FCSTD DOCUMENT  (FreeCAD 0.18R16131 (Git))
Label: Plattform
License: All rights reserved
LicenseURL: http://en.wikipedia.org/wiki/All_rights_reserved
objects: App::Part×1, Spreadsheet::Sheet×1, Sketcher::SketchObject×1
note: 1 computed .brp shape members not serialized (recipe doc carries the construction recipe); baked Part::Feature solids carry a one-line shape summary decoded from their .brp

FEATURE [App::Part] Part
  Origin = -> Origin
FEATURE [Spreadsheet::Sheet] Spreadsheet
  cells = E1=Schlitze; A2=length; B2=330; C2=MountholeRadius; D2=3.1; E2=lenght; F2=20; A3=width; B3=200; E3=width; F3=3.1
FEATURE [Sketcher::SketchObject] Sketch
  expr: Constraints[516] = Spreadsheet.F2
  expr: Constraints[195] = Spreadsheet.F2
  expr: Constraints[4] = Spreadsheet.B2
  expr: Constraints[3] = Spreadsheet.B3
  expr: Constraints[515] = Spreadsheet.F3
  expr: Constraints[179] = Spreadsheet.F3
  expr: Constraints[20] = Spreadsheet.D2
  sketch-geometry (180):
    g0: LineSegment StartX=-200 StartY=370 StartZ=0 EndX=-200 EndY=40 EndZ=0
    g1: LineSegment StartX=-2.84e-14 StartY=370 StartZ=0 EndX=-1.137e-13 EndY=40 EndZ=0
    g2: ArcOfCircle CenterX=-100 CenterY=191.667 CenterZ=0 NormalX=0 NormalY=0 NormalZ=1 AngleXU=0 Radius=181.667 StartAngle=4.12948 EndAngle=5.2953
    g3: GeomPoint X=-100 Y=10 Z=0
    g4: ArcOfCircle CenterX=-100 CenterY=265 CenterZ=0 NormalX=0 NormalY=0 NormalZ=1 AngleXU=0 Radius=145 StartAngle=0.809784 EndAngle=2.33181
    g5: GeomPoint X=-100 Y=410 Z=0
    g6: Circle CenterX=-140.9 CenterY=65 CenterZ=0 NormalX=0 NormalY=0 NormalZ=1 AngleXU=0 Radius=3.1
    g7: Circle CenterX=-58.1 CenterY=65 CenterZ=0 NormalX=0 NormalY=0 NormalZ=1 AngleXU=0 Radius=3.1
    g8: Circle CenterX=-135 CenterY=366.2 CenterZ=0 NormalX=0 NormalY=0 NormalZ=1 AngleXU=0 Radius=3.1
    g9: Circle CenterX=-65 CenterY=366.2 CenterZ=0 NormalX=0 NormalY=0 NormalZ=1 AngleXU=0 Radius=3.1
    g10: Circle CenterX=-114 CenterY=195.2 CenterZ=0 NormalX=0 NormalY=0 NormalZ=1 AngleXU=0 Radius=2.1
    g11: Circle CenterX=-74 CenterY=195.2 CenterZ=0 NormalX=0 NormalY=0 NormalZ=1 AngleXU=0 Radius=10
    g12: LineSegment StartX=-180 StartY=310 StartZ=0 EndX=-160 EndY=310 EndZ=0
    g13: LineSegment StartX=-160 StartY=310 StartZ=0 EndX=-160 EndY=306.9 EndZ=0
    g14: LineSegment StartX=-160 StartY=306.9 StartZ=0 EndX=-180 EndY=306.9 EndZ=0
    g15: LineSegment StartX=-180 StartY=306.9 StartZ=0 EndX=-180 EndY=310 EndZ=0
    g16: LineSegment StartX=-40 StartY=310 StartZ=0 EndX=-20 EndY=310 EndZ=0
    g17: LineSegment StartX=-20 StartY=310 StartZ=0 EndX=-20 EndY=306.9 EndZ=0
    g18: LineSegment StartX=-20 StartY=306.9 StartZ=0 EndX=-40 EndY=306.9 EndZ=0
    g19: LineSegment StartX=-40 StartY=306.9 StartZ=0 EndX=-40 EndY=310 EndZ=0
    g20: LineSegment StartX=-180 StartY=280 StartZ=0 EndX=-160 EndY=280 EndZ=0
    g21: LineSegment StartX=-160 StartY=280 StartZ=0 EndX=-160 EndY=276.9 EndZ=0
    g22: LineSegment StartX=-160 StartY=276.9 StartZ=0 EndX=-180 EndY=276.9 EndZ=0
    g23: LineSegment StartX=-180 StartY=276.9 StartZ=0 EndX=-180 EndY=280 EndZ=0
    g24: LineSegment StartX=-180 StartY=340 StartZ=0 EndX=-160 EndY=340 EndZ=0
    g25: LineSegment StartX=-160 StartY=340 StartZ=0 EndX=-160 EndY=336.9 EndZ=0
    g26: LineSegment StartX=-160 StartY=336.9 StartZ=0 EndX=-180 EndY=336.9 EndZ=0
    g27: LineSegment StartX=-180 StartY=336.9 StartZ=0 EndX=-180 EndY=340 EndZ=0
    g28: LineSegment StartX=-40 StartY=340 StartZ=0 EndX=-20 EndY=340 EndZ=0
    g29: LineSegment StartX=-20 StartY=340 StartZ=0 EndX=-20 EndY=336.9 EndZ=0
    g30: LineSegment StartX=-20 StartY=336.9 StartZ=0 EndX=-40 EndY=336.9 EndZ=0
    g31: LineSegment StartX=-40 StartY=336.9 StartZ=0 EndX=-40 EndY=340 EndZ=0
    g32: LineSegment StartX=-40 StartY=280 StartZ=0 EndX=-20 EndY=280 EndZ=0
    g33: LineSegment StartX=-20 StartY=280 StartZ=0 EndX=-20 EndY=276.9 EndZ=0
    g34: LineSegment StartX=-20 StartY=276.9 StartZ=0 EndX=-40 EndY=276.9 EndZ=0
    g35: LineSegment StartX=-40 StartY=276.9 StartZ=0 EndX=-40 EndY=280 EndZ=0
    g36: LineSegment StartX=-180 StartY=370 StartZ=0 EndX=-160 EndY=370 EndZ=0
    g37: LineSegment StartX=-160 StartY=370 StartZ=0 EndX=-160 EndY=366.9 EndZ=0
    g38: LineSegment StartX=-160 StartY=366.9 StartZ=0 EndX=-180 EndY=366.9 EndZ=0
    g39: LineSegment StartX=-180 StartY=366.9 StartZ=0 EndX=-180 EndY=370 EndZ=0
    g40: LineSegment StartX=-40 StartY=370 StartZ=0 EndX=-20 EndY=370 EndZ=0
    g41: LineSegment StartX=-20 StartY=370 StartZ=0 EndX=-20 EndY=366.9 EndZ=0
    g42: LineSegment StartX=-20 StartY=366.9 StartZ=0 EndX=-40 EndY=366.9 EndZ=0
    g43: LineSegment StartX=-40 StartY=366.9 StartZ=0 EndX=-40 EndY=370 EndZ=0
    g44: LineSegment StartX=-180 StartY=250 StartZ=0 EndX=-160 EndY=250 EndZ=0
    g45: LineSegment StartX=-160 StartY=250 StartZ=0 EndX=-160 EndY=246.9 EndZ=0
    g46: LineSegment StartX=-160 StartY=246.9 StartZ=0 EndX=-180 EndY=246.9 EndZ=0
    g47: LineSegment StartX=-180 StartY=246.9 StartZ=0 EndX=-180 EndY=250 EndZ=0
    g48: LineSegment StartX=-40 StartY=246.9 StartZ=0 EndX=-20 EndY=246.9 EndZ=0
    g49: LineSegment StartX=-20 StartY=246.9 StartZ=0 EndX=-20 EndY=250 EndZ=0
    g50: LineSegment StartX=-20 StartY=250 StartZ=0 EndX=-40 EndY=250 EndZ=0
    g51: LineSegment StartX=-40 StartY=250 StartZ=0 EndX=-40 EndY=246.9 EndZ=0
    g52: LineSegment StartX=-180 StartY=220 StartZ=0 EndX=-160 EndY=220 EndZ=0
    g53: LineSegment StartX=-160 StartY=220 StartZ=0 EndX=-160 EndY=216.9 EndZ=0
    g54: LineSegment StartX=-160 StartY=216.9 StartZ=0 EndX=-180 EndY=216.9 EndZ=0
    g55: LineSegment StartX=-180 StartY=216.9 StartZ=0 EndX=-180 EndY=220 EndZ=0
    g56: LineSegment StartX=-40 StartY=220 StartZ=0 EndX=-20 EndY=220 EndZ=0
    g57: LineSegment StartX=-20 StartY=220 StartZ=0 EndX=-20 EndY=216.9 EndZ=0
    g58: LineSegment StartX=-20 StartY=216.9 StartZ=0 EndX=-40 EndY=216.9 EndZ=0
    g59: LineSegment StartX=-40 StartY=216.9 StartZ=0 EndX=-40 EndY=220 EndZ=0
    g60: LineSegment StartX=-180 StartY=190 StartZ=0 EndX=-160 EndY=190 EndZ=0
    g61: LineSegment StartX=-160 StartY=190 StartZ=0 EndX=-160 EndY=186.9 EndZ=0
    g62: LineSegment StartX=-160 StartY=186.9 StartZ=0 EndX=-180 EndY=186.9 EndZ=0
    g63: LineSegment StartX=-180 StartY=186.9 StartZ=0 EndX=-180 EndY=190 EndZ=0
    g64: LineSegment StartX=-40 StartY=190 StartZ=0 EndX=-20 EndY=190 EndZ=0
    g65: LineSegment StartX=-20 StartY=190 StartZ=0 EndX=-20 EndY=186.9 EndZ=0
    g66: LineSegment StartX=-20 StartY=186.9 StartZ=0 EndX=-40 EndY=186.9 EndZ=0
    g67: LineSegment StartX=-40 StartY=186.9 StartZ=0 EndX=-40 EndY=190 EndZ=0
    g68: LineSegment StartX=-180 StartY=160 StartZ=0 EndX=-160 EndY=160 EndZ=0
    g69: LineSegment StartX=-160 StartY=160 StartZ=0 EndX=-160 EndY=156.9 EndZ=0
    g70: LineSegment StartX=-160 StartY=156.9 StartZ=0 EndX=-180 EndY=156.9 EndZ=0
    g71: LineSegment StartX=-180 StartY=156.9 StartZ=0 EndX=-180 EndY=160 EndZ=0
    g72: LineSegment StartX=-40 StartY=160 StartZ=0 EndX=-20 EndY=160 EndZ=0
    g73: LineSegment StartX=-20 StartY=160 StartZ=0 EndX=-20 EndY=156.9 EndZ=0
    g74: LineSegment StartX=-20 StartY=156.9 StartZ=0 EndX=-40 EndY=156.9 EndZ=0
    g75: LineSegment StartX=-40 StartY=156.9 StartZ=0 EndX=-40 EndY=160 EndZ=0
    g76: LineSegment StartX=-180 StartY=40 StartZ=0 EndX=-160 EndY=40 EndZ=0
    g77: LineSegment StartX=-160 StartY=40 StartZ=0 EndX=-160 EndY=36.9 EndZ=0
    g78: LineSegment StartX=-160 StartY=36.9 StartZ=0 EndX=-180 EndY=36.9 EndZ=0
    g79: LineSegment StartX=-180 StartY=36.9 StartZ=0 EndX=-180 EndY=40 EndZ=0
    g80: LineSegment StartX=-40 StartY=40 StartZ=0 EndX=-20 EndY=40 EndZ=0
    g81: LineSegment StartX=-20 StartY=40 StartZ=0 EndX=-20 EndY=36.9 EndZ=0
    g82: LineSegment StartX=-20 StartY=36.9 StartZ=0 EndX=-40 EndY=36.9 EndZ=0
    g83: LineSegment StartX=-40 StartY=36.9 StartZ=0 EndX=-40 EndY=40 EndZ=0
    g84: LineSegment StartX=-180 StartY=130 StartZ=0 EndX=-160 EndY=130 EndZ=0
    g85: LineSegment StartX=-160 StartY=130 StartZ=0 EndX=-160 EndY=126.9 EndZ=0
    g86: LineSegment StartX=-160 StartY=126.9 StartZ=0 EndX=-180 EndY=126.9 EndZ=0
    g87: LineSegment StartX=-180 StartY=126.9 StartZ=0 EndX=-180 EndY=130 EndZ=0
    g88: LineSegment StartX=-180 StartY=100 StartZ=0 EndX=-160 EndY=100 EndZ=0
    g89: LineSegment StartX=-160 StartY=100 StartZ=0 EndX=-160 EndY=96.9 EndZ=0
    g90: LineSegment StartX=-160 StartY=96.9 StartZ=0 EndX=-180 EndY=96.9 EndZ=0
    g91: LineSegment StartX=-180 StartY=96.9 StartZ=0 EndX=-180 EndY=100 EndZ=0
    g92: LineSegment StartX=-180 StartY=70 StartZ=0 EndX=-160 EndY=70 EndZ=0
    g93: LineSegment StartX=-160 StartY=70 StartZ=0 EndX=-160 EndY=66.9 EndZ=0
    g94: LineSegment StartX=-160 StartY=66.9 StartZ=0 EndX=-180 EndY=66.9 EndZ=0
    g95: LineSegment StartX=-180 StartY=66.9 StartZ=0 EndX=-180 EndY=70 EndZ=0
    g96: LineSegment StartX=-40 StartY=130 StartZ=0 EndX=-20 EndY=130 EndZ=0
    g97: LineSegment StartX=-20 StartY=130 StartZ=0 EndX=-20 EndY=126.9 EndZ=0
    g98: LineSegment StartX=-20 StartY=126.9 StartZ=0 EndX=-40 EndY=126.9 EndZ=0
    g99: LineSegment StartX=-40 StartY=126.9 StartZ=0 EndX=-40 EndY=130 EndZ=0
    g100: LineSegment StartX=-40 StartY=100 StartZ=0 EndX=-20 EndY=100 EndZ=0
    g101: LineSegment StartX=-20 StartY=100 StartZ=0 EndX=-20 EndY=96.9 EndZ=0
    g102: LineSegment StartX=-20 StartY=96.9 StartZ=0 EndX=-40 EndY=96.9 EndZ=0
    g103: LineSegment StartX=-40 StartY=96.9 StartZ=0 EndX=-40 EndY=100 EndZ=0
    g104: LineSegment StartX=-40 StartY=70 StartZ=0 EndX=-20 EndY=70 EndZ=0
    g105: LineSegment StartX=-20 StartY=70 StartZ=0 EndX=-20 EndY=66.9 EndZ=0
    g106: LineSegment StartX=-20 StartY=66.9 StartZ=0 EndX=-40 EndY=66.9 EndZ=0
    g107: LineSegment StartX=-40 StartY=66.9 StartZ=0 EndX=-40 EndY=70 EndZ=0
    g108: LineSegment StartX=-116.55 StartY=40 StartZ=0 EndX=-113.45 EndY=40 EndZ=0
    g109: LineSegment StartX=-113.45 StartY=40 StartZ=0 EndX=-113.45 EndY=20 EndZ=0
    g110: LineSegment StartX=-113.45 StartY=20 StartZ=0 EndX=-116.55 EndY=20 EndZ=0
    g111: LineSegment StartX=-116.55 StartY=20 StartZ=0 EndX=-116.55 EndY=40 EndZ=0
    g112: LineSegment StartX=-86.55 StartY=40 StartZ=0 EndX=-83.45 EndY=40 EndZ=0
    g113: LineSegment StartX=-83.45 StartY=40 StartZ=0 EndX=-83.45 EndY=20 EndZ=0
    g114: LineSegment StartX=-83.45 StartY=20 StartZ=0 EndX=-86.55 EndY=20 EndZ=0
    g115: LineSegment StartX=-86.55 StartY=20 StartZ=0 EndX=-86.55 EndY=40 EndZ=0
    g116: LineSegment StartX=-116.55 StartY=90 StartZ=0 EndX=-113.45 EndY=90 EndZ=0
    g117: LineSegment StartX=-113.45 StartY=90 StartZ=0 EndX=-113.45 EndY=70 EndZ=0
    g118: LineSegment StartX=-113.45 StartY=70 StartZ=0 EndX=-116.55 EndY=70 EndZ=0
    g119: LineSegment StartX=-116.55 StartY=70 StartZ=0 EndX=-116.55 EndY=90 EndZ=0
    g120: LineSegment StartX=-116.55 StartY=140 StartZ=0 EndX=-113.45 EndY=140 EndZ=0
    g121: LineSegment StartX=-113.45 StartY=140 StartZ=0 EndX=-113.45 EndY=120 EndZ=0
    g122: LineSegment StartX=-113.45 StartY=120 StartZ=0 EndX=-116.55 EndY=120 EndZ=0
    g123: LineSegment StartX=-116.55 StartY=120 StartZ=0 EndX=-116.55 EndY=140 EndZ=0
    g124: LineSegment StartX=-116.55 StartY=190 StartZ=0 EndX=-113.45 EndY=190 EndZ=0
    g125: LineSegment StartX=-113.45 StartY=190 StartZ=0 EndX=-113.45 EndY=170 EndZ=0
    g126: LineSegment StartX=-113.45 StartY=170 StartZ=0 EndX=-116.55 EndY=170 EndZ=0
    g127: LineSegment StartX=-116.55 StartY=170 StartZ=0 EndX=-116.55 EndY=190 EndZ=0
    g128: LineSegment StartX=-86.55 StartY=90 StartZ=0 EndX=-83.45 EndY=90 EndZ=0
    g129: LineSegment StartX=-83.45 StartY=90 StartZ=0 EndX=-83.45 EndY=70 EndZ=0
    g130: LineSegment StartX=-83.45 StartY=70 StartZ=0 EndX=-86.55 EndY=70 EndZ=0
    g131: LineSegment StartX=-86.55 StartY=70 StartZ=0 EndX=-86.55 EndY=90 EndZ=0
    g132: LineSegment StartX=-86.55 StartY=140 StartZ=0 EndX=-83.45 EndY=140 EndZ=0
    g133: LineSegment StartX=-83.45 StartY=140 StartZ=0 EndX=-83.45 EndY=120 EndZ=0
    g134: LineSegment StartX=-83.45 StartY=120 StartZ=0 EndX=-86.55 EndY=120 EndZ=0
    g135: LineSegment StartX=-86.55 StartY=120 StartZ=0 EndX=-86.55 EndY=140 EndZ=0
    g136: LineSegment StartX=-86.55 StartY=190 StartZ=0 EndX=-83.45 EndY=190 EndZ=0
    g137: LineSegment StartX=-83.45 StartY=190 StartZ=0 EndX=-83.45 EndY=170 EndZ=0
    g138: LineSegment StartX=-83.45 StartY=170 StartZ=0 EndX=-86.55 EndY=170 EndZ=0
    g139: LineSegment StartX=-86.55 StartY=170 StartZ=0 EndX=-86.55 EndY=190 EndZ=0
    g140: LineSegment StartX=-116.55 StartY=270 StartZ=0 EndX=-113.45 EndY=270 EndZ=0
    g141: LineSegment StartX=-113.45 StartY=270 StartZ=0 EndX=-113.45 EndY=250 EndZ=0
    g142: LineSegment StartX=-113.45 StartY=250 StartZ=0 EndX=-116.55 EndY=250 EndZ=0
    g143: LineSegment StartX=-116.55 StartY=250 StartZ=0 EndX=-116.55 EndY=270 EndZ=0
    g144: LineSegment StartX=-86.55 StartY=270 StartZ=0 EndX=-83.45 EndY=270 EndZ=0
    g145: LineSegment StartX=-83.45 StartY=270 StartZ=0 EndX=-83.45 EndY=250 EndZ=0
    g146: LineSegment StartX=-83.45 StartY=250 StartZ=0 EndX=-86.55 EndY=250 EndZ=0
    g147: LineSegment StartX=-86.55 StartY=250 StartZ=0 EndX=-86.55 EndY=270 EndZ=0
    g148: LineSegment StartX=-116.55 StartY=320 StartZ=0 EndX=-113.45 EndY=320 EndZ=0
    g149: LineSegment StartX=-113.45 StartY=320 StartZ=0 EndX=-113.45 EndY=300 EndZ=0
    g150: LineSegment StartX=-113.45 StartY=300 StartZ=0 EndX=-116.55 EndY=300 EndZ=0
    g151: LineSegment StartX=-116.55 StartY=300 StartZ=0 EndX=-116.55 EndY=320 EndZ=0
    g152: LineSegment StartX=-86.55 StartY=320 StartZ=0 EndX=-83.45 EndY=320 EndZ=0
    g153: LineSegment StartX=-83.45 StartY=320 StartZ=0 EndX=-83.45 EndY=300 EndZ=0
    g154: LineSegment StartX=-83.45 StartY=300 StartZ=0 EndX=-86.55 EndY=300 EndZ=0
    g155: LineSegment StartX=-86.55 StartY=300 StartZ=0 EndX=-86.55 EndY=320 EndZ=0
    g156: LineSegment StartX=-116.55 StartY=405 StartZ=0 EndX=-113.45 EndY=405 EndZ=0
    g157: LineSegment StartX=-113.45 StartY=405 StartZ=0 EndX=-113.45 EndY=385 EndZ=0
    g158: LineSegment StartX=-113.45 StartY=385 StartZ=0 EndX=-116.55 EndY=385 EndZ=0
    g159: LineSegment StartX=-116.55 StartY=385 StartZ=0 EndX=-116.55 EndY=405 EndZ=0
    g160: LineSegment StartX=-86.55 StartY=405 StartZ=0 EndX=-83.45 EndY=405 EndZ=0
    g161: LineSegment StartX=-83.45 StartY=405 StartZ=0 EndX=-83.45 EndY=385 EndZ=0
    g162: LineSegment StartX=-83.45 StartY=385 StartZ=0 EndX=-86.55 EndY=385 EndZ=0
    g163: LineSegment StartX=-86.55 StartY=385 StartZ=0 EndX=-86.55 EndY=405 EndZ=0
    g164: LineSegment StartX=-116.55 StartY=370 StartZ=0 EndX=-113.45 EndY=370 EndZ=0
    g165: LineSegment StartX=-113.45 StartY=370 StartZ=0 EndX=-113.45 EndY=350 EndZ=0
    g166: LineSegment StartX=-113.45 StartY=350 StartZ=0 EndX=-116.55 EndY=350 EndZ=0
    g167: LineSegment StartX=-116.55 StartY=350 StartZ=0 EndX=-116.55 EndY=370 EndZ=0
    g168: LineSegment StartX=-86.55 StartY=370 StartZ=0 EndX=-83.45 EndY=370 EndZ=0
    g169: LineSegment StartX=-83.45 StartY=370 StartZ=0 EndX=-83.45 EndY=350 EndZ=0
    g170: LineSegment StartX=-83.45 StartY=350 StartZ=0 EndX=-86.55 EndY=350 EndZ=0
    g171: LineSegment StartX=-86.55 StartY=350 StartZ=0 EndX=-86.55 EndY=370 EndZ=0
    g172: LineSegment StartX=-150 StartY=399.183 StartZ=0 EndX=-50 EndY=399.183 EndZ=0
    g173: LineSegment StartX=-150 StartY=396.183 StartZ=0 EndX=-50 EndY=396.183 EndZ=0
    g174: LineSegment StartX=-150 StartY=399.183 StartZ=0 EndX=-150 EndY=396.183 EndZ=0
    g175: LineSegment StartX=-50 StartY=399.183 StartZ=0 EndX=-50 EndY=396.183 EndZ=0
    g176: LineSegment StartX=-199.37 StartY=369.621 StartZ=0 EndX=-198.001 EndY=367.341 EndZ=0
    g177: LineSegment StartX=-199.37 StartY=369.621 StartZ=0 EndX=-151.545 EndY=398.755 EndZ=0
    g178: LineSegment StartX=-198.001 StartY=367.341 StartZ=0 EndX=-150 EndY=396.183 EndZ=0
    g179: LineSegment StartX=-151.545 StartY=398.755 StartZ=0 EndX=-150 EndY=396.183 EndZ=0
  constraints (538):
    c: Parallel(g1,g0)
    c: Angle(g1) = -1.5708
    c: DistanceX(g1,g-1) = 0
    c: DistanceX(g0,g1) = 200
    c: DistanceY(g1,g1) = 330
    c: DistanceY(g-1,g1) = 40
    c: DistanceY(g0,g1) = 0
    c: Coincident(g2,g0)
    c: Coincident(g2,g1)
    c: PointOnObject(g3,g2)
    c: DistanceY(g-1,g3) = 10
    c: DistanceX(g3,g-1) = 100
    c: Coincident(g4,g0)
    c: Coincident(g4,g1)
    c: PointOnObject(g5,g4)
    c: DistanceX(g5,g-1) = 100
    c: DistanceY(g1,g5) = 40
    c: Equal(g6,g8)
    c: Equal(g8,g9)
    c: Equal(g9,g7)
    c: Radius(g6) = 3.1
    c: DistanceX(g6,g7) = 82.8
    c: DistanceX(g3,g7) = 41.9
    c: DistanceY(g1,g7) = 25
    c: DistanceY(g7,g6) = 0
    c: DistanceX(g8,g9) = 70
    c: DistanceY(g8,g9) = 0
    c: DistanceX(g3,g9) = 35
    c: DistanceY(g6,g8) = 301.2
    c: Radius(g10) = 2.1
    c: DistanceX(g0,g10) = 86
    c: DistanceY(g6,g10) = 130.2
    c: Radius(g11) = 10
    c: DistanceY(g11,g10) = 0
    c: DistanceX(g10,g11) = 40
    c: Coincident(g12,g13)
    c: Coincident(g13,g14)
    c: Coincident(g14,g15)
    c: Coincident(g15,g12)
    c: Horizontal(g12)
    c: Horizontal(g14)
    c: Vertical(g13)
    c: Vertical(g15)
    c: Coincident(g16,g17)
    c: Coincident(g17,g18)
    c: Coincident(g18,g19)
    c: Coincident(g19,g16)
    c: Horizontal(g16)
    c: Horizontal(g18)
    c: Vertical(g17)
    c: Vertical(g19)
    c: Coincident(g20,g21)
    c: Coincident(g21,g22)
    c: Coincident(g22,g23)
    c: Coincident(g23,g20)
    c: Horizontal(g20)
    c: Horizontal(g22)
    c: Vertical(g21)
    c: Vertical(g23)
    c: Coincident(g24,g25)
    c: Coincident(g25,g26)
    c: Coincident(g26,g27)
    c: Coincident(g27,g24)
    c: Horizontal(g24)
    c: Horizontal(g26)
    c: Vertical(g25)
    c: Vertical(g27)
    c: Coincident(g28,g29)
    c: Coincident(g29,g30)
    c: Coincident(g30,g31)
    c: Coincident(g31,g28)
    c: Horizontal(g28)
    c: Horizontal(g30)
    c: Vertical(g29)
    c: Vertical(g31)
    c: Coincident(g32,g33)
    c: Coincident(g33,g34)
    c: Coincident(g34,g35)
    c: Coincident(g35,g32)
    c: Horizontal(g32)
    c: Horizontal(g34)
    c: Vertical(g33)
    c: Vertical(g35)
    c: Coincident(g36,g37)
    c: Coincident(g37,g38)
    c: Coincident(g38,g39)
    c: Coincident(g39,g36)
    c: Horizontal(g36)
    c: Horizontal(g38)
    c: Vertical(g37)
    c: Vertical(g39)
    c: Coincident(g40,g41)
    c: Coincident(g41,g42)
    c: Coincident(g42,g43)
    c: Coincident(g43,g40)
    c: Horizontal(g40)
    c: Horizontal(g42)
    c: Vertical(g41)
    c: Vertical(g43)
    c: Coincident(g44,g45)
    c: Coincident(g45,g46)
    c: Coincident(g46,g47)
    c: Coincident(g47,g44)
    c: Horizontal(g44)
    c: Horizontal(g46)
    c: Vertical(g45)
    c: Vertical(g47)
    c: Coincident(g48,g49)
    c: Coincident(g49,g50)
    c: Coincident(g50,g51)
    c: Coincident(g51,g48)
    c: Horizontal(g48)
    c: Horizontal(g50)
    c: Vertical(g49)
    c: Vertical(g51)
    c: Coincident(g52,g53)
    c: Coincident(g53,g54)
    c: Coincident(g54,g55)
    c: Coincident(g55,g52)
    c: Horizontal(g52)
    c: Horizontal(g54)
    c: Vertical(g53)
    c: Vertical(g55)
    c: Coincident(g56,g57)
    c: Coincident(g57,g58)
    c: Coincident(g58,g59)
    c: Coincident(g59,g56)
    c: Horizontal(g56)
    c: Horizontal(g58)
    c: Vertical(g57)
    c: Vertical(g59)
    c: Coincident(g60,g61)
    c: Coincident(g61,g62)
    c: Coincident(g62,g63)
    c: Coincident(g63,g60)
    c: Horizontal(g60)
    c: Horizontal(g62)
    c: Vertical(g61)
    c: Vertical(g63)
    c: Coincident(g64,g65)
    c: Coincident(g65,g66)
    c: Coincident(g66,g67)
    c: Coincident(g67,g64)
    c: Horizontal(g64)
    c: Horizontal(g66)
    c: Vertical(g65)
    c: Vertical(g67)
    c: Coincident(g68,g69)
    c: Coincident(g69,g70)
    c: Coincident(g70,g71)
    c: Coincident(g71,g68)
    c: Horizontal(g68)
    c: Horizontal(g70)
    c: Vertical(g69)
    c: Vertical(g71)
    c: Coincident(g72,g73)
    c: Coincident(g73,g74)
    c: Coincident(g74,g75)
    c: Coincident(g75,g72)
    c: Horizontal(g72)
    c: Horizontal(g74)
    c: Vertical(g73)
    c: Vertical(g75)
    c: Coincident(g76,g77)
    c: Coincident(g77,g78)
    c: Coincident(g78,g79)
    c: Coincident(g79,g76)
    c: Horizontal(g76)
    c: Horizontal(g78)
    c: Vertical(g77)
    c: Vertical(g79)
    c: Coincident(g80,g81)
    c: Coincident(g81,g82)
    c: Coincident(g82,g83)
    c: Coincident(g83,g80)
    c: Horizontal(g80)
    c: Horizontal(g82)
    c: Vertical(g81)
    c: Vertical(g83)
    c: DistanceY(g39,g39) = 3.1
    c: Equal(g39,g27)
    c: Equal(g27,g15)
    c: Equal(g15,g43)
    c: Equal(g43,g31)
    c: Equal(g31,g19)
    c: Equal(g19,g35)
    c: Equal(g35,g23)
    c: Equal(g23,g47)
    c: Equal(g47,g51)
    c: Equal(g51,g55)
    c: Equal(g55,g59)
    c: Equal(g59,g63)
    c: Equal(g63,g67)
    c: Equal(g67,g71)
    c: Equal(g71,g75)
    c: DistanceX(g36,g36) = 20
    c: Equal(g36,g40)
    c: Equal(g40,g24)
    c: Equal(g24,g28)
    c: Equal(g28,g12)
    c: Equal(g12,g16)
    c: Equal(g16,g20)
    c: Equal(g20,g32)
    c: Equal(g32,g44)
    c: Equal(g44,g48)
    c: Equal(g48,g52)
    c: Equal(g52,g56)
    c: Equal(g56,g60)
    c: Equal(g60,g64)
    c: Equal(g64,g68)
    c: Equal(g68,g72)
    c: Equal(g72,g76)
    c: Equal(g76,g80)
    c: Equal(g71,g79)
    c: Equal(g79,g83)
    c: DistanceX(g0,g38) = 20
    c: DistanceX(g38,g26) = 0
    c: DistanceX(g26,g14) = 0
    c: DistanceX(g14,g22) = 0
    c: DistanceX(g22,g46) = 0
    c: DistanceX(g46,g54) = 0
    c: DistanceX(g54,g62) = 0
    c: DistanceX(g62,g70) = 0
    c: DistanceX(g70,g78) = 0
    c: DistanceX(g41,g1) = 20
    c: DistanceX(g29,g41) = 0
    c: DistanceX(g17,g29) = 0
    c: DistanceX(g33,g17) = 0
    c: DistanceX(g49,g33) = 0
    c: DistanceX(g57,g49) = 0
    c: DistanceX(g65,g57) = 0
    c: DistanceX(g73,g65) = 0
    c: DistanceY(g36,g0) = 0
    c: DistanceY(g40,g1) = 0
    c: DistanceY(g24,g36) = 30
    c: DistanceY(g20,g12) = 30
    c: DistanceY(g44,g20) = 30
    c: DistanceY(g52,g44) = 30
    c: DistanceY(g60,g52) = 30
    c: DistanceY(g68,g60) = 30
    c: DistanceY(g28,g40) = 30
    c: DistanceY(g16,g28) = 30
    c: DistanceY(g32,g16) = 30
    c: DistanceY(g64,g56) = 30
    c: DistanceY(g56,g49) = 30
    c: DistanceY(g72,g64) = 30
    c: DistanceY(g49,g32) = 30
    c: DistanceY(g12,g24) = 30
    c: Coincident(g84,g85)
    c: Coincident(g85,g86)
    c: Coincident(g86,g87)
    c: Coincident(g87,g84)
    c: Horizontal(g84)
    c: Horizontal(g86)
    c: Vertical(g85)
    c: Vertical(g87)
    c: Coincident(g88,g89)
    c: Coincident(g89,g90)
    c: Coincident(g90,g91)
    c: Coincident(g91,g88)
    c: Horizontal(g88)
    c: Horizontal(g90)
    c: Vertical(g89)
    c: Vertical(g91)
    c: Coincident(g92,g93)
    c: Coincident(g93,g94)
    c: Coincident(g94,g95)
    c: Coincident(g95,g92)
    c: Horizontal(g92)
    c: Horizontal(g94)
    c: Vertical(g93)
    c: Vertical(g95)
    c: Coincident(g96,g97)
    c: Coincident(g97,g98)
    c: Coincident(g98,g99)
    c: Coincident(g99,g96)
    c: Horizontal(g96)
    c: Horizontal(g98)
    c: Vertical(g97)
    c: Vertical(g99)
    c: Coincident(g100,g101)
    c: Coincident(g101,g102)
    c: Coincident(g102,g103)
    c: Coincident(g103,g100)
    c: Horizontal(g100)
    c: Vertical(g101)
    c: Vertical(g103)
    c: Coincident(g104,g105)
    c: Coincident(g105,g106)
    c: Coincident(g106,g107)
    c: Coincident(g107,g104)
    c: Horizontal(g104)
    c: Horizontal(g106)
    c: Vertical(g105)
    c: Vertical(g107)
    c: Equal(g75,g99)
    c: Equal(g99,g103)
    c: Equal(g95,g91)
    c: Equal(g91,g87)
    c: Equal(g68,g84)
    c: Equal(g84,g88)
    c: Equal(g88,g96)
    c: Equal(g96,g100)
    c: Equal(g104,g92)
    c: DistanceX(g68,g84) = 0
    c: DistanceX(g84,g88) = 0
    c: DistanceX(g88,g92) = 0
    c: DistanceX(g96,g72) = 0
    c: DistanceX(g100,g96) = 0
    c: DistanceY(g96,g72) = 30
    c: DistanceY(g100,g96) = 30
    c: DistanceY(g104,g100) = 30
    c: DistanceY(g80,g104) = 30
    c: DistanceY(g84,g68) = 30
    c: DistanceY(g88,g84) = 30
    c: DistanceY(g92,g88) = 30
    c: Equal(g105,g81)
    c: Equal(g81,g101)
    c: DistanceX(g104,g100) = 0
    c: DistanceX(g104,g80) = 0
    c: Equal(g104,g100)
    c: DistanceY(g0,g1) = 0
    c: DistanceY(g76,g92) = 30
    c: Equal(g91,g87)
    c: Equal(g89,g61)
    c: Coincident(g108,g109)
    c: Coincident(g109,g110)
    c: Coincident(g110,g111)
    c: Coincident(g111,g108)
    c: Horizontal(g108)
    c: Horizontal(g110)
    c: Vertical(g109)
    c: Vertical(g111)
    c: Coincident(g112,g113)
    c: Coincident(g113,g114)
    c: Coincident(g114,g115)
    c: Coincident(g115,g112)
    c: Horizontal(g112)
    c: Horizontal(g114)
    c: Vertical(g113)
    c: Vertical(g115)
    c: Coincident(g116,g117)
    c: Coincident(g117,g118)
    c: Coincident(g118,g119)
    c: Coincident(g119,g116)
    c: Horizontal(g116)
    c: Horizontal(g118)
    c: Vertical(g117)
    c: Vertical(g119)
    c: Coincident(g120,g121)
    c: Coincident(g121,g122)
    c: Coincident(g122,g123)
    c: Coincident(g123,g120)
    c: Horizontal(g120)
    c: Horizontal(g122)
    c: Vertical(g121)
    c: Vertical(g123)
    c: Coincident(g124,g125)
    c: Coincident(g125,g126)
    c: Coincident(g126,g127)
    c: Coincident(g127,g124)
    c: Horizontal(g124)
    c: Horizontal(g126)
    c: Vertical(g125)
    c: Vertical(g127)
    c: Coincident(g128,g129)
    c: Coincident(g129,g130)
    c: Coincident(g130,g131)
    c: Coincident(g131,g128)
    c: Horizontal(g128)
    c: Horizontal(g130)
    c: Vertical(g129)
    c: Vertical(g131)
    c: Coincident(g132,g133)
    c: Coincident(g133,g134)
    c: Coincident(g134,g135)
    c: Coincident(g135,g132)
    c: Horizontal(g132)
    c: Horizontal(g134)
    c: Vertical(g133)
    c: Vertical(g135)
    c: Coincident(g136,g137)
    c: Coincident(g137,g138)
    c: Coincident(g138,g139)
    c: Coincident(g139,g136)
    c: Horizontal(g136)
    c: Horizontal(g138)
    c: Vertical(g137)
    c: Vertical(g139)
    c: Coincident(g140,g141)
    c: Coincident(g141,g142)
    c: Coincident(g142,g143)
    c: Coincident(g143,g140)
    c: Horizontal(g140)
    c: Horizontal(g142)
    c: Vertical(g141)
    c: Vertical(g143)
    c: Coincident(g144,g145)
    c: Coincident(g145,g146)
    c: Coincident(g146,g147)
    c: Coincident(g147,g144)
    c: Horizontal(g144)
    c: Horizontal(g146)
    c: Vertical(g145)
    c: Vertical(g147)
    c: Coincident(g148,g149)
    c: Coincident(g149,g150)
    c: Coincident(g150,g151)
    c: Coincident(g151,g148)
    c: Horizontal(g148)
    c: Horizontal(g150)
    c: Vertical(g149)
    c: Vertical(g151)
    c: Coincident(g152,g153)
    c: Coincident(g153,g154)
    c: Coincident(g154,g155)
    c: Coincident(g155,g152)
    c: Horizontal(g152)
    c: Horizontal(g154)
    c: Vertical(g153)
    c: Vertical(g155)
    c: Coincident(g156,g157)
    c: Coincident(g157,g158)
    c: Coincident(g158,g159)
    c: Coincident(g159,g156)
    c: Horizontal(g156)
    c: Horizontal(g158)
    c: Vertical(g157)
    c: Vertical(g159)
    c: Coincident(g160,g161)
    c: Coincident(g161,g162)
    c: Coincident(g162,g163)
    c: Coincident(g163,g160)
    c: Horizontal(g160)
    c: Horizontal(g162)
    c: Vertical(g161)
    c: Vertical(g163)
    c: Coincident(g164,g165)
    c: Coincident(g165,g166)
    c: Coincident(g166,g167)
    c: Coincident(g167,g164)
    c: Horizontal(g164)
    c: Horizontal(g166)
    c: Vertical(g165)
    c: Vertical(g167)
    c: Coincident(g168,g169)
    c: Coincident(g169,g170)
    c: Coincident(g170,g171)
    c: Coincident(g171,g168)
    c: Horizontal(g168)
    c: Horizontal(g170)
    c: Vertical(g169)
    c: Vertical(g171)
    c: Equal(g111,g115)
    c: Equal(g115,g131)
    c: Equal(g131,g119)
    c: Equal(g119,g123)
    c: Equal(g123,g135)
    c: Equal(g135,g127)
    c: Equal(g127,g139)
    c: Equal(g139,g147)
    c: Equal(g147,g143)
    c: Equal(g143,g151)
    c: Equal(g151,g155)
    c: Equal(g155,g163)
    c: Equal(g163,g159)
    c: Equal(g159,g167)
    c: Equal(g167,g171)
    c: Equal(g110,g114)
    c: Equal(g114,g118)
    c: Equal(g118,g130)
    c: Equal(g130,g122)
    c: Equal(g122,g134)
    c: Equal(g134,g138)
    c: Equal(g138,g126)
    c: Equal(g126,g142)
    c: Equal(g142,g146)
    c: Equal(g146,g154)
    c: Equal(g154,g150)
    c: Equal(g150,g158)
    c: Equal(g158,g162)
    c: Equal(g162,g166)
    c: Equal(g166,g170)
    c: DistanceY(g164,g0) = 0
    c: DistanceY(g168,g1) = 0
    c: DistanceX(g164,g168) = 30
    c: DistanceX(g168,g1) = 86.55
    c: DistanceX(g156,g160) = 30
    c: DistanceY(g156,g160) = 0
    c: DistanceX(g148,g152) = 30
    c: DistanceY(g152,g148) = 0
    c: DistanceX(g140,g144) = 30
    c: DistanceY(g140,g144) = 0
    c: DistanceX(g124,g136) = 30
    c: DistanceY(g136,g124) = 0
    c: DistanceX(g120,g132) = 30
    c: DistanceY(g132,g120) = 0
    c: DistanceX(g116,g128) = 30
    c: DistanceY(g128,g116) = 0
    c: DistanceX(g108,g112) = 30
    c: DistanceY(g112,g108) = 0
    c: DistanceX(g161,g168) = 0
    c: DistanceY(g168,g161) = 15
    c: DistanceX(g116,g108) = 0
    c: DistanceX(g120,g116) = 0
    c: DistanceX(g120,g124) = 0
    c: DistanceX(g124,g140) = 0
    c: DistanceX(g148,g140) = 0
    c: DistanceX(g148,g166) = 0
    c: DistanceY(g1,g112) = 0
    c: DistanceY(g152,g169) = 30
    c: DistanceY(g144,g153) = 30
    c: DistanceY(g112,g129) = 30
    c: DistanceY(g128,g133) = 30
    c: DistanceY(g132,g137) = 30
    c: DistanceX(g110,g110) = 3.1
    c: DistanceY(g109,g109) = 20
    c: Coincident(g173,g175)
    c: Coincident(g172,g175)
    c: Coincident(g172,g174)
    c: Coincident(g173,g174)
    c: Coincident(g177,g176)
    c: Coincident(g178,g176)
    c: Coincident(g177,g179)
    c: Coincident(g178,g179)
    c: Angle(g173) = 0
    c: Perpendicular(g175,g173)
    c: Parallel(g173,g172)
    c: Parallel(g175,g174)
    c: Equal(g178,g177)
    c: Perpendicular(g179,g178)
    c: Distance(g178) = 56
    c: Distance(g179) = 3
    c: Angle(g178) = 0.541052
    c: DistanceY(g174,g174) = 3
    c: DistanceX(g172,g172) = 100
    c: Coincident(g178,g173)
    c: DistanceX(g173,g-1) = 50
